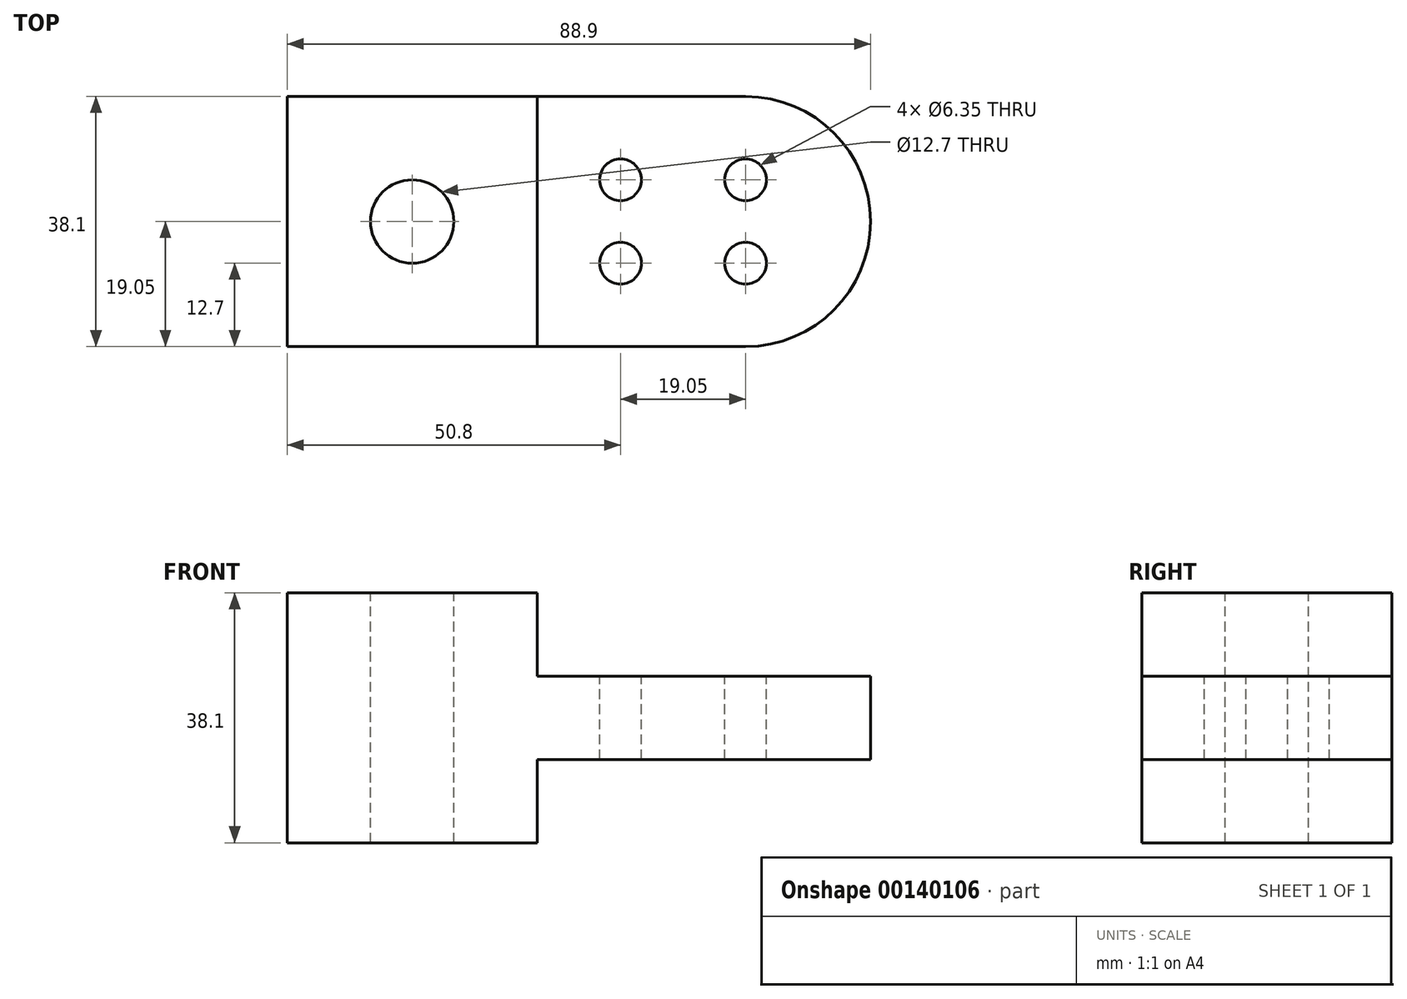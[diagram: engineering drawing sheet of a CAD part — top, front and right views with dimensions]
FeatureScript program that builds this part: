
annotation { "Feature Type Name" : "Feature", "Feature Type Description" : "" }
export const myFeature = defineFeature(function(context is Context, id is Id, definition is map)
    precondition{}
    {
        {
            var Q0;
            Q0=qCreatedBy(makeId("Front.planeOp"),FACE);
            var sketch = newSketch(context, id + "F0", { "sketchPlane" : qUnion([Q0])});
            skLineSegment(sketch, "E0", {"start": v(0, 0) * mm, "end": v(0, 38.1) * mm});
            skLineSegment(sketch, "E1", {"start": v(0, 38.1) * mm, "end": v(38.1, 38.1) * mm});
            skLineSegment(sketch, "E2", {"start": v(38.1, 38.1) * mm, "end": v(38.1, 25.4) * mm});
            skLineSegment(sketch, "E3", {"start": v(38.1, 25.4) * mm, "end": v(88.9, 25.4) * mm});
            skLineSegment(sketch, "E4", {"start": v(88.9, 25.4) * mm, "end": v(88.9, 12.7) * mm});
            skLineSegment(sketch, "E5", {"start": v(88.9, 12.7) * mm, "end": v(38.1, 12.7) * mm});
            skLineSegment(sketch, "E6", {"start": v(38.1, 12.7) * mm, "end": v(38.1, 0) * mm});
            skLineSegment(sketch, "E7", {"start": v(38.1, 0) * mm, "end": v(0, 0) * mm});
            skSolve(sketch);
        }
        {
            var Q0;
            Q0 = qSketchRegion(id + "F0", true);
            extrude(context, id + "F1", {"entities" : qUnion([Q0]), "depth" : 38.1 * mm});
        }
        {
            var Q0;
            Q0=makeQuery(id+"F1.opExtrude","SWEPT_FACE",FACE,{"disambiguationData":[OSD([sQuery(id+"F0.wireOp",EDGE,"E3")])]});
            var sketch = newSketch(context, id + "F2", { "sketchPlane" : qUnion([Q0])});
            skArc(sketch, "E8", {"start": v(69.85, -38.1) * mm, "mid": v(88.9, -19.05) * mm, "end": v(69.85, 0) * mm});
            skLineSegment(sketch, "E9.0", {"start": v(88.9, -38.1) * mm, "end": v(88.9, 0) * mm});
            skLineSegment(sketch, "E10.0", {"start": v(38.1, 0) * mm, "end": v(88.9, 0) * mm});
            skLineSegment(sketch, "E11.0", {"start": v(38.1, -38.1) * mm, "end": v(88.9, -38.1) * mm});
            skSolve(sketch);
        }
        {
            var Q0;
            {var subQ0=sQuery(id+"F2.wireOp",EDGE,"E11.0");var subQ1=sQuery(id+"F2.wireOp",EDGE,"E8");var subQ2=makeQuery(id+"F2.imprint","INTERSECT",VERTEX,{"derivedFrom":[subQ1,subQ0]});Q0=makeQuery(id+"F2.imprint","IMPRINT",FACE,{"disambiguationData":[TD([[makeQuery(id+"F2.imprint","IMPRINT",EDGE,{"disambiguationData":[TD([[subQ2,-1.0]])],"derivedFrom":subQ1}),-1.0]])]});}
            var Q1;
            {var subQ0=sQuery(id+"F2.wireOp",EDGE,"E10.0");var subQ1=sQuery(id+"F2.wireOp",EDGE,"E8");var subQ2=makeQuery(id+"F2.imprint","INTERSECT",VERTEX,{"derivedFrom":[subQ1,subQ0]});Q1=makeQuery(id+"F2.imprint","IMPRINT",FACE,{"disambiguationData":[TD([[makeQuery(id+"F2.imprint","IMPRINT",EDGE,{"disambiguationData":[TD([[subQ2,1.0]])],"derivedFrom":subQ1}),-1.0]])]});}
            extrude(context, id + "F3", {"entities" : qUnion([Q0, Q1]), "operationType" : NewBodyOperationType.REMOVE, "oppositeDirection" : true, "depth" : 25.4 * mm});
        }
        {
            var Q0;
            Q0=makeQuery(id+"F1.opExtrude","SWEPT_FACE",FACE,{"disambiguationData":[OSD([sQuery(id+"F0.wireOp",EDGE,"E3")])]});
            var sketch = newSketch(context, id + "F4", { "sketchPlane" : qUnion([Q0])});
            skLineSegment(sketch, "E12", {"start": v(38.1, -12.7) * mm, "end": v(88.96, -12.7) * mm, "construction": true});
            skLineSegment(sketch, "E13", {"start": v(38.1, -25.4) * mm, "end": v(101.86, -25.4) * mm, "construction": true});
            skLineSegment(sketch, "E14", {"start": v(50.8, 1.56) * mm, "end": v(50.8, -46.5) * mm, "construction": true});
            skLineSegment(sketch, "E15", {"start": v(69.85, 2.07) * mm, "end": v(69.85, -43.86) * mm, "construction": true});
            skCircle(sketch, "E16", {"center": v(69.85, -12.7) * mm, "radius": 3.18 * mm});
            skCircle(sketch, "E17", {"center": v(69.85, -25.4) * mm, "radius": 3.18 * mm});
            skCircle(sketch, "E18", {"center": v(50.8, -25.4) * mm, "radius": 3.18 * mm});
            skCircle(sketch, "E19", {"center": v(50.8, -12.7) * mm, "radius": 3.18 * mm});
            skSolve(sketch);
        }
        {
            var Q0;
            Q0 = qSketchRegion(id + "F4", true);
            extrude(context, id + "F5", {"entities" : qUnion([Q0]), "operationType" : NewBodyOperationType.REMOVE, "oppositeDirection" : true, "depth" : 25.4 * mm});
        }
        {
            var Q0;
            Q0=makeQuery(id+"F1.opExtrude","SWEPT_FACE",FACE,{"disambiguationData":[OSD([sQuery(id+"F0.wireOp",EDGE,"E1")])]});
            var sketch = newSketch(context, id + "F6", { "sketchPlane" : qUnion([Q0])});
            skCircle(sketch, "E20", {"center": v(19.05, -19.05) * mm, "radius": 6.35 * mm});
            skSolve(sketch);
        }
        {
            var Q0;
            Q0 = qSketchRegion(id + "F6", true);
            extrude(context, id + "F7", {"entities" : qUnion([Q0]), "operationType" : NewBodyOperationType.REMOVE, "oppositeDirection" : true, "depth" : 63.87 * mm});
        }
    });
